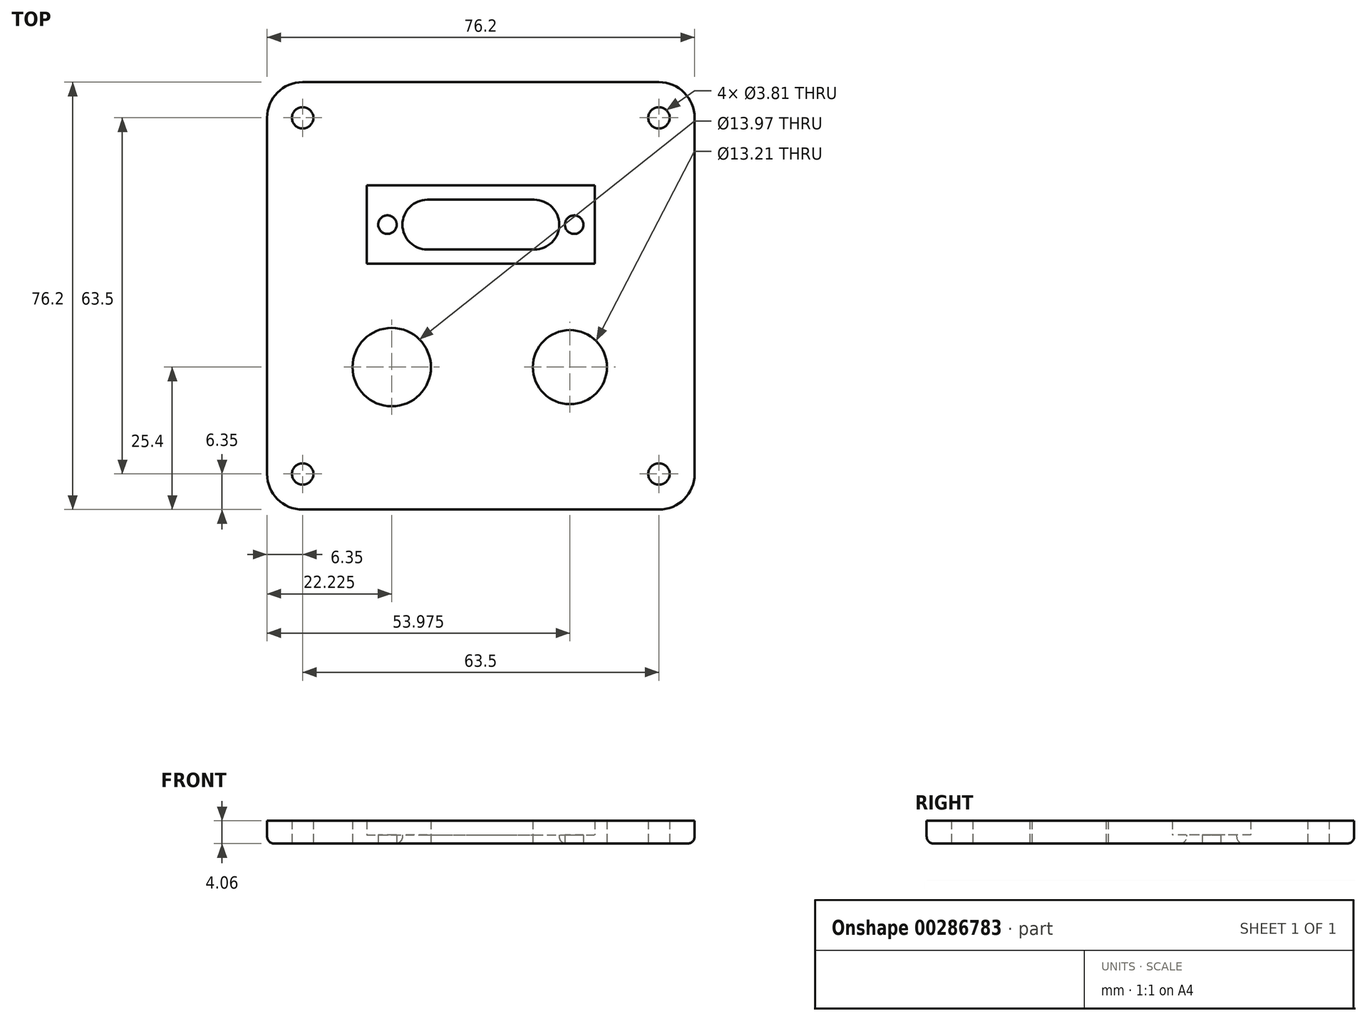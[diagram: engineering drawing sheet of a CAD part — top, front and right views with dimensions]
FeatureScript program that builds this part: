
annotation { "Feature Type Name" : "Feature", "Feature Type Description" : "" }
export const myFeature = defineFeature(function(context is Context, id is Id, definition is map)
    precondition{}
    {
        {
            var Q0;
            Q0=qCreatedBy(makeId("Top.planeOp"),FACE);
            var sketch = newSketch(context, id + "F0", { "sketchPlane" : qUnion([Q0])});
            skCircle(sketch, "E0", {"center": v(-16.64, 0) * mm, "radius": 1.65 * mm});
            skCircle(sketch, "E1", {"center": v(16.64, 0) * mm, "radius": 1.65 * mm});
            skLineSegment(sketch, "E2", {"start": v(-16.64, 0) * mm, "end": v(16.64, 0) * mm, "construction": true});
            skPoint(sketch, "E3", {"position": v(0, 0) * mm});
            skLineSegment(sketch, "E4", {"start": v(-9.53, 4.44) * mm, "end": v(9.53, 4.44) * mm});
            skLineSegment(sketch, "E5", {"start": v(9.53, -4.44) * mm, "end": v(-9.53, -4.44) * mm});
            skArc(sketch, "E6", {"start": v(-9.53, 4.44) * mm, "mid": v(-13.97, 0) * mm, "end": v(-9.53, -4.44) * mm});
            skArc(sketch, "E7", {"start": v(9.53, -4.44) * mm, "mid": v(13.97, 0) * mm, "end": v(9.53, 4.44) * mm});
            skPoint(sketch, "E8", {"position": v(0, 4.44) * mm});
            skLineSegment(sketch, "E9.bottom", {"start": v(-38.1, 25.4) * mm, "end": v(38.1, 25.4) * mm});
            skLineSegment(sketch, "E9.top", {"start": v(-38.1, -50.8) * mm, "end": v(38.1, -50.8) * mm});
            skLineSegment(sketch, "E9.left", {"start": v(-38.1, 25.4) * mm, "end": v(-38.1, -50.8) * mm});
            skLineSegment(sketch, "E9.right", {"start": v(38.1, 25.4) * mm, "end": v(38.1, -50.8) * mm});
            skPoint(sketch, "E10", {"position": v(0, 25.4) * mm});
            skLineSegment(sketch, "E11", {"start": v(0, 0) * mm, "end": v(0, -25.4) * mm, "construction": true});
            skPoint(sketch, "E12", {"position": v(0, -12.7) * mm});
            skPoint(sketch, "E13", {"position": v(38.1, -12.7) * mm});
            skCircle(sketch, "E14", {"center": v(-31.75, 19.05) * mm, "radius": 1.9 * mm});
            skCircle(sketch, "E15", {"center": v(31.75, 19.05) * mm, "radius": 1.9 * mm});
            skCircle(sketch, "E16", {"center": v(31.75, -44.45) * mm, "radius": 1.9 * mm});
            skCircle(sketch, "E17", {"center": v(-31.75, -44.45) * mm, "radius": 1.9 * mm});
            skLineSegment(sketch, "E18", {"start": v(-31.75, 19.05) * mm, "end": v(-31.75, 25.4) * mm, "construction": true});
            skLineSegment(sketch, "E19", {"start": v(-31.75, 19.05) * mm, "end": v(-38.1, 19.05) * mm, "construction": true});
            skLineSegment(sketch, "E20", {"start": v(-31.75, -44.45) * mm, "end": v(-31.75, -50.8) * mm, "construction": true});
            skLineSegment(sketch, "E21", {"start": v(31.75, -44.45) * mm, "end": v(38.1, -44.45) * mm, "construction": true});
            skLineSegment(sketch, "E22", {"start": v(-15.88, -25.4) * mm, "end": v(15.88, -25.4) * mm, "construction": true});
            skPoint(sketch, "E23", {"position": v(0, -25.4) * mm});
            skCircle(sketch, "E24", {"center": v(-15.88, -25.4) * mm, "radius": 6.99 * mm});
            skCircle(sketch, "E25", {"center": v(15.88, -25.4) * mm, "radius": 6.6 * mm});
            skSolve(sketch);
        }
        {
            var Q0;
            Q0 = qSketchRegion(id + "F0", true);
            extrude(context, id + "F1", {"entities" : qUnion([Q0]), "depth" : 1.52 * mm});
        }
        {
            var Q0;
            Q0=makeQuery(id+"F1.opExtrude","CAP_FACE",FACE,{"disambiguationData":[OSD([sQuery(id+"F0.wireOp",EDGE,"E0"),sQuery(id+"F0.wireOp",EDGE,"E1"),sQuery(id+"F0.wireOp",EDGE,"E4"),sQuery(id+"F0.wireOp",EDGE,"E5"),sQuery(id+"F0.wireOp",EDGE,"E6"),sQuery(id+"F0.wireOp",EDGE,"E7"),sQuery(id+"F0.wireOp",EDGE,"E9.bottom"),sQuery(id+"F0.wireOp",EDGE,"E9.top"),sQuery(id+"F0.wireOp",EDGE,"E9.left"),sQuery(id+"F0.wireOp",EDGE,"E9.right"),sQuery(id+"F0.wireOp",EDGE,"3HXjpLeM-deta-KMb6-UrGM-dHZJc7QnA8EO"),sQuery(id+"F0.wireOp",EDGE,"E14"),sQuery(id+"F0.wireOp",EDGE,"E15"),sQuery(id+"F0.wireOp",EDGE,"E16"),sQuery(id+"F0.wireOp",EDGE,"E17")])],"isStart":false});
            var sketch = newSketch(context, id + "F2", { "sketchPlane" : qUnion([Q0])});
            skLineSegment(sketch, "E26.bottom", {"start": v(-38.1, 25.4) * mm, "end": v(38.1, 25.4) * mm});
            skLineSegment(sketch, "E26.top", {"start": v(-38.1, -50.8) * mm, "end": v(38.1, -50.8) * mm});
            skLineSegment(sketch, "E26.left", {"start": v(-38.1, 25.4) * mm, "end": v(-38.1, -50.8) * mm});
            skLineSegment(sketch, "E26.right", {"start": v(38.1, 25.4) * mm, "end": v(38.1, -50.8) * mm});
            skCircle(sketch, "E27", {"center": v(-31.75, -44.45) * mm, "radius": 1.9 * mm});
            skCircle(sketch, "E28", {"center": v(-31.75, 19.05) * mm, "radius": 1.9 * mm});
            skCircle(sketch, "E29", {"center": v(31.75, 19.05) * mm, "radius": 1.9 * mm});
            skCircle(sketch, "E30", {"center": v(31.75, -44.45) * mm, "radius": 1.9 * mm});
            skLineSegment(sketch, "E31.bottom", {"start": v(-20.32, 6.99) * mm, "end": v(20.32, 6.98) * mm});
            skLineSegment(sketch, "E31.top", {"start": v(-20.32, -6.98) * mm, "end": v(20.32, -6.99) * mm});
            skLineSegment(sketch, "E31.left", {"start": v(-20.32, 6.99) * mm, "end": v(-20.32, -6.99) * mm});
            skLineSegment(sketch, "E31.right", {"start": v(20.32, 6.99) * mm, "end": v(20.32, -6.99) * mm});
            skPoint(sketch, "E32", {"position": v(0, 6.99) * mm});
            skPoint(sketch, "E33", {"position": v(-20.32, 0) * mm});
            skSolve(sketch);
        }
        {
            var Q0;
            Q0 = qSketchRegion(id + "F2", true);
            extrude(context, id + "F3", {"entities" : qUnion([Q0]), "operationType" : NewBodyOperationType.ADD, "depth" : 2.54 * mm});
        }
        {
            var Q0;
            Q0=makeQuery(id+"F3.boolean.opBoolean","MERGE",EDGE,{"derivedFrom":[makeQuery(id+"F1.opExtrude","SWEPT_EDGE",EDGE,{"disambiguationData":[OSD([sQuery(id+"F0.wireOp",EDGE,"E9.top"),sQuery(id+"F0.wireOp",EDGE,"E9.left")])]}),makeQuery(id+"F3.opExtrude","SWEPT_EDGE",EDGE,{"disambiguationData":[OSD([sQuery(id+"F2.wireOp",EDGE,"E26.top"),sQuery(id+"F2.wireOp",EDGE,"E26.left")])]})]});
            var Q1;
            Q1=makeQuery(id+"F3.boolean.opBoolean","MERGE",EDGE,{"derivedFrom":[makeQuery(id+"F1.opExtrude","SWEPT_EDGE",EDGE,{"disambiguationData":[OSD([sQuery(id+"F0.wireOp",EDGE,"E9.top"),sQuery(id+"F0.wireOp",EDGE,"E9.right")])]}),makeQuery(id+"F3.opExtrude","SWEPT_EDGE",EDGE,{"disambiguationData":[OSD([sQuery(id+"F2.wireOp",EDGE,"E26.top"),sQuery(id+"F2.wireOp",EDGE,"E26.right")])]})]});
            var Q2;
            Q2=makeQuery(id+"F3.boolean.opBoolean","MERGE",EDGE,{"derivedFrom":[makeQuery(id+"F1.opExtrude","SWEPT_EDGE",EDGE,{"disambiguationData":[OSD([sQuery(id+"F0.wireOp",EDGE,"E9.bottom"),sQuery(id+"F0.wireOp",EDGE,"E9.left")])]}),makeQuery(id+"F3.opExtrude","SWEPT_EDGE",EDGE,{"disambiguationData":[OSD([sQuery(id+"F2.wireOp",EDGE,"E26.bottom"),sQuery(id+"F2.wireOp",EDGE,"E26.left")])]})]});
            var Q3;
            Q3=makeQuery(id+"F3.boolean.opBoolean","MERGE",EDGE,{"derivedFrom":[makeQuery(id+"F1.opExtrude","SWEPT_EDGE",EDGE,{"disambiguationData":[OSD([sQuery(id+"F0.wireOp",EDGE,"E9.bottom"),sQuery(id+"F0.wireOp",EDGE,"E9.right")])]}),makeQuery(id+"F3.opExtrude","SWEPT_EDGE",EDGE,{"disambiguationData":[OSD([sQuery(id+"F2.wireOp",EDGE,"E26.bottom"),sQuery(id+"F2.wireOp",EDGE,"E26.right")])]})]});
            fillet(context, id + "F4", {"entities" : qUnion([Q0, Q1, Q2, Q3]), "radius" : 6.35 * mm, "tangentPropagation" : true, "allowEdgeOverflow" : false});
        }
        {
            var Q0;
            {var subQ0=sQuery(id+"F0.wireOp",EDGE,"E9.left");var subQ1=sQuery(id+"F0.wireOp",EDGE,"E9.top");Q0=makeQuery(id+"F4.opFillet","BLEND_EDGE",EDGE,{"blendedFrom":[makeQuery(id+"F3.boolean.opBoolean","MERGE",EDGE,{"derivedFrom":[makeQuery(id+"F1.opExtrude","SWEPT_EDGE",EDGE,{"disambiguationData":[OSD([subQ1,subQ0])]}),makeQuery(id+"F3.opExtrude","SWEPT_EDGE",EDGE,{"disambiguationData":[OSD([sQuery(id+"F2.wireOp",EDGE,"E26.top"),sQuery(id+"F2.wireOp",EDGE,"E26.left")])]})]}),makeQuery(id+"F1.opExtrude","CAP_FACE",FACE,{"disambiguationData":[OSD([sQuery(id+"F0.wireOp",EDGE,"E0"),sQuery(id+"F0.wireOp",EDGE,"E1"),sQuery(id+"F0.wireOp",EDGE,"E4"),sQuery(id+"F0.wireOp",EDGE,"E5"),sQuery(id+"F0.wireOp",EDGE,"E6"),sQuery(id+"F0.wireOp",EDGE,"E7"),sQuery(id+"F0.wireOp",EDGE,"E9.bottom"),subQ1,subQ0,sQuery(id+"F0.wireOp",EDGE,"E9.right"),sQuery(id+"F0.wireOp",EDGE,"3HXjpLeM-deta-KMb6-UrGM-dHZJc7QnA8EO"),sQuery(id+"F0.wireOp",EDGE,"E14"),sQuery(id+"F0.wireOp",EDGE,"E15"),sQuery(id+"F0.wireOp",EDGE,"E16"),sQuery(id+"F0.wireOp",EDGE,"E17")])],"isStart":true})],"blendedInto":[makeQuery(id+"F1.opExtrude","CAP_FACE",FACE,{"disambiguationData":[OSD([sQuery(id+"F0.wireOp",EDGE,"E0"),sQuery(id+"F0.wireOp",EDGE,"E1"),sQuery(id+"F0.wireOp",EDGE,"E4"),sQuery(id+"F0.wireOp",EDGE,"E5"),sQuery(id+"F0.wireOp",EDGE,"E6"),sQuery(id+"F0.wireOp",EDGE,"E7"),sQuery(id+"F0.wireOp",EDGE,"E9.bottom"),subQ1,subQ0,sQuery(id+"F0.wireOp",EDGE,"E9.right"),sQuery(id+"F0.wireOp",EDGE,"3HXjpLeM-deta-KMb6-UrGM-dHZJc7QnA8EO"),sQuery(id+"F0.wireOp",EDGE,"E14"),sQuery(id+"F0.wireOp",EDGE,"E15"),sQuery(id+"F0.wireOp",EDGE,"E16"),sQuery(id+"F0.wireOp",EDGE,"E17")])],"isStart":true})]});}
            var Q1;
            Q1=makeQuery(id+"F1.opExtrude","CAP_EDGE",EDGE,{"disambiguationData":[OSD([sQuery(id+"F0.wireOp",EDGE,"E4")])],"isStart":true});
            var Q2;
            Q2=makeQuery(id+"F1.opExtrude","CAP_EDGE",EDGE,{"disambiguationData":[OSD([sQuery(id+"F0.wireOp",EDGE,"3HXjpLeM-deta-KMb6-UrGM-dHZJc7QnA8EO")])],"isStart":true});
            fillet(context, id + "F5", {"entities" : qUnion([Q0, Q1, Q2]), "radius" : 1.27 * mm, "tangentPropagation" : true, "allowEdgeOverflow" : false});
        }
        {
            var Q0;
            Q0=makeQuery(id+"F3.boolean.opBoolean","SPLIT",FACE,{"disambiguationData":[TD([makeQuery(id+"F1.opExtrude","SWEPT_FACE",FACE,{"disambiguationData":[OSD([sQuery(id+"F0.wireOp",EDGE,"E25")])]})])],"derivedFrom":makeQuery(id+"F3.opExtrude","CAP_FACE",FACE,{"disambiguationData":[OSD([sQuery(id+"F2.wireOp",EDGE,"E26.bottom"),sQuery(id+"F2.wireOp",EDGE,"E26.top"),sQuery(id+"F2.wireOp",EDGE,"E26.left"),sQuery(id+"F2.wireOp",EDGE,"E26.right"),sQuery(id+"F2.wireOp",EDGE,"E27"),sQuery(id+"F2.wireOp",EDGE,"E28"),sQuery(id+"F2.wireOp",EDGE,"E29"),sQuery(id+"F2.wireOp",EDGE,"E30"),sQuery(id+"F2.wireOp",EDGE,"E31.bottom"),sQuery(id+"F2.wireOp",EDGE,"E31.top"),sQuery(id+"F2.wireOp",EDGE,"E31.left"),sQuery(id+"F2.wireOp",EDGE,"E31.right")])],"isStart":true})});
            var Q1;
            Q1=makeQuery(id+"F3.boolean.opBoolean","SPLIT",FACE,{"disambiguationData":[TD([makeQuery(id+"F1.opExtrude","SWEPT_FACE",FACE,{"disambiguationData":[OSD([sQuery(id+"F0.wireOp",EDGE,"E24")])]})])],"derivedFrom":makeQuery(id+"F3.opExtrude","CAP_FACE",FACE,{"disambiguationData":[OSD([sQuery(id+"F2.wireOp",EDGE,"E26.bottom"),sQuery(id+"F2.wireOp",EDGE,"E26.top"),sQuery(id+"F2.wireOp",EDGE,"E26.left"),sQuery(id+"F2.wireOp",EDGE,"E26.right"),sQuery(id+"F2.wireOp",EDGE,"E27"),sQuery(id+"F2.wireOp",EDGE,"E28"),sQuery(id+"F2.wireOp",EDGE,"E29"),sQuery(id+"F2.wireOp",EDGE,"E30"),sQuery(id+"F2.wireOp",EDGE,"E31.bottom"),sQuery(id+"F2.wireOp",EDGE,"E31.top"),sQuery(id+"F2.wireOp",EDGE,"E31.left"),sQuery(id+"F2.wireOp",EDGE,"E31.right")])],"isStart":true})});
            var Q2;
            Q2=makeQuery(id+"F3.opExtrude","CAP_FACE",FACE,{"disambiguationData":[OSD([sQuery(id+"F2.wireOp",EDGE,"E26.bottom"),sQuery(id+"F2.wireOp",EDGE,"E26.top"),sQuery(id+"F2.wireOp",EDGE,"E26.left"),sQuery(id+"F2.wireOp",EDGE,"E26.right"),sQuery(id+"F2.wireOp",EDGE,"E27"),sQuery(id+"F2.wireOp",EDGE,"E28"),sQuery(id+"F2.wireOp",EDGE,"E29"),sQuery(id+"F2.wireOp",EDGE,"E30"),sQuery(id+"F2.wireOp",EDGE,"E31.bottom"),sQuery(id+"F2.wireOp",EDGE,"E31.top"),sQuery(id+"F2.wireOp",EDGE,"E31.left"),sQuery(id+"F2.wireOp",EDGE,"E31.right")])],"isStart":false});
            extrude(context, id + "F6", {"entities" : qUnion([Q0, Q1]), "operationType" : NewBodyOperationType.REMOVE, "endBound" : BoundingType.UP_TO_SURFACE, "oppositeDirection" : true, "depth" : 25.4 * mm, "endBoundEntityFace" : qUnion([Q2]), "offsetDistance" : 25.4 * mm});
        }
    });
